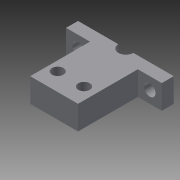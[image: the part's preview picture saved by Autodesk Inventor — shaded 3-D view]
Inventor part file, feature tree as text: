
AUTODESK INVENTOR PART (.ipt)
format: ipt  version: 2015 (Build 190159000, 159)  size: 134,144 bytes
history: native  units: in
note: dims shown in document units (in); Inventor stores cm internally (conversion verified against a paired STEP export)
features: extrude x4, sketch x2
ambient origin geometry x8: Origin, YZ Plane, XZ Plane, XY Plane, X Axis, Y Axis, Z Axis, Center Point
bodies: Body1 (feature_tree)
feature tree (6):
  sketch  "Sketch1"  dims[d0=0.248in d6=0.5906in]
  extrude  "Extrusion10"  Depth=0.5906in
  extrude  "Extrusion11"  Depth=0.3937in
  sketch  "Sketch3"  dims[d34=0.3543in d35=0.3937in d36=0.1969in d37=0.3937in d38=0.1969in d43=0.1969in d44=0.1969in d45=0.1772in d46=0.1772in d47=0.1772in d48=0.1772in d49=0.3937in d50=0.0in d51=0.1969in d52=0.0in d53=0.1969in d54=0.1969in d55=0.1969in d56=0.1969in d57=0.185in d58=0.185in d61=0.189in d62=0.189in d63=0.3937in d64=0.0in d65=0.189in d66=0.189in d67=0.3937in d68=0.0in]
  extrude  "Extrusion13"  Depth=0.1969in
  extrude  "Extrusion14"  Depth=0.3937in
